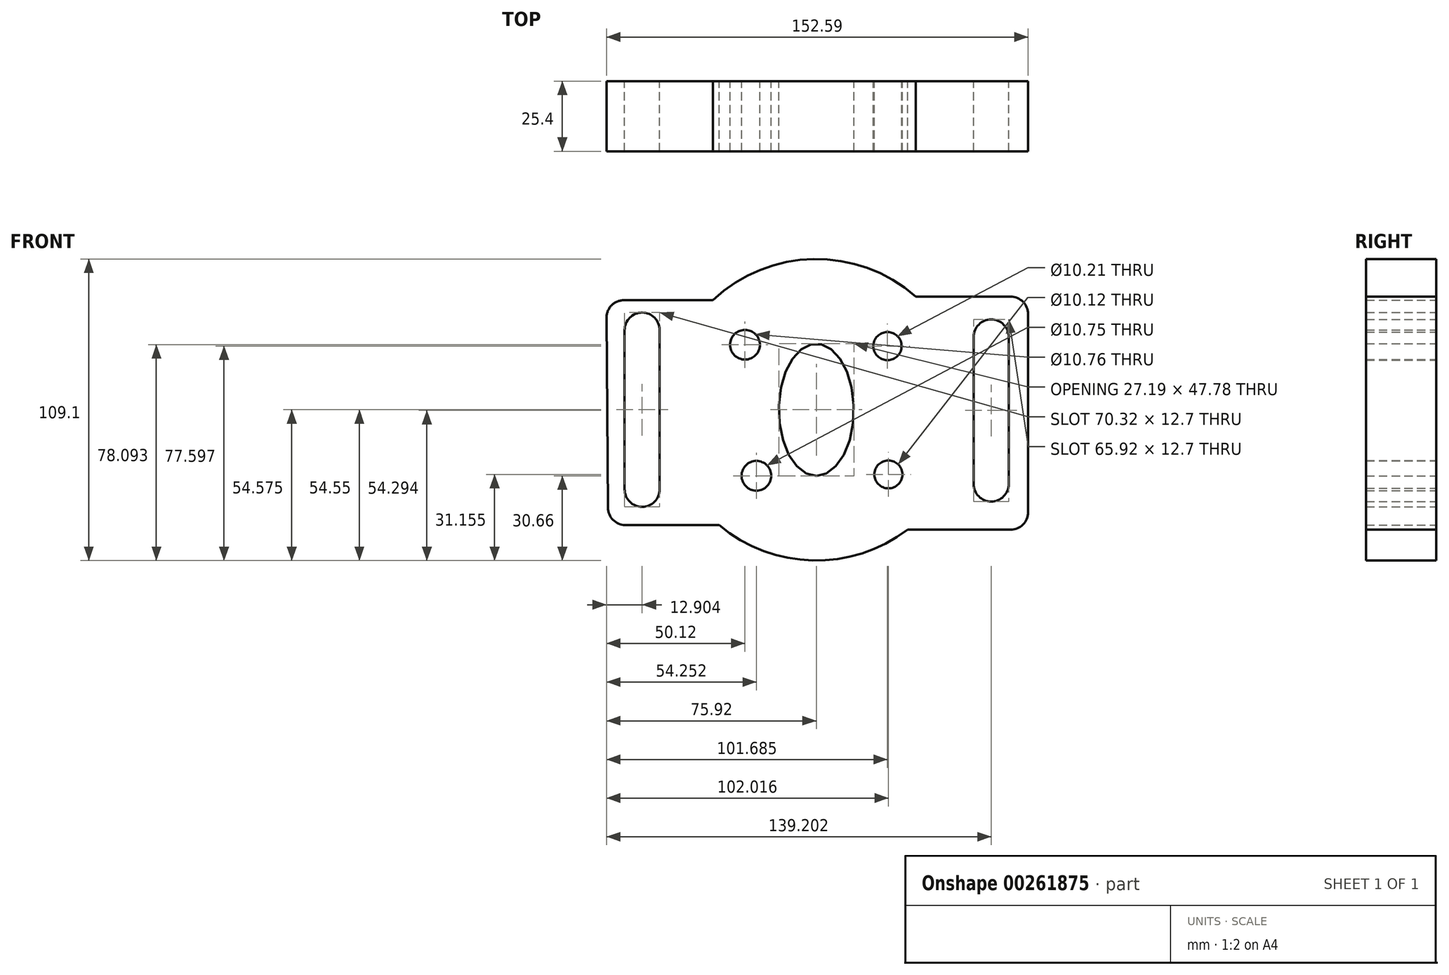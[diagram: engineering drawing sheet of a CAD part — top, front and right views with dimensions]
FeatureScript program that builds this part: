
annotation { "Feature Type Name" : "Feature", "Feature Type Description" : "" }
export const myFeature = defineFeature(function(context is Context, id is Id, definition is map)
    precondition{}
    {
        {
            var Q0;
            Q0=qCreatedBy(makeId("Front.planeOp"),FACE);
            var sketch = newSketch(context, id + "F0", { "sketchPlane" : qUnion([Q0])});
            skEllipse(sketch, "E0", {"center": v(0, 0) * mm, "majorRadius": 23.9 * mm, "minorRadius": 13.6 * mm, "majorAxis": v(0, -1)});
            skCircle(sketch, "E1", {"center": v(25.77, 23.05) * mm, "radius": 5.1 * mm});
            skCircle(sketch, "E2", {"center": v(26.1, -23.4) * mm, "radius": 5.06 * mm});
            skCircle(sketch, "E3", {"center": v(-21.67, -23.9) * mm, "radius": 5.38 * mm});
            skCircle(sketch, "E4", {"center": v(-25.8, 23.54) * mm, "radius": 5.38 * mm});
            skArc(sketch, "E5", {"start": v(36.05, 40.94) * mm, "mid": v(-0.94, 54.54) * mm, "end": v(-37.43, 39.68) * mm});
            skLineSegment(sketch, "E6", {"start": v(36.05, 40.94) * mm, "end": v(70.32, 40.94) * mm});
            skLineSegment(sketch, "E7", {"start": v(76.67, 34.59) * mm, "end": v(76.67, -37.04) * mm});
            skLineSegment(sketch, "E8", {"start": v(70.32, -43.4) * mm, "end": v(33.06, -43.4) * mm});
            skLineSegment(sketch, "E9", {"start": v(63.28, 26.35) * mm, "end": v(63.28, -26.87) * mm});
            skArc(sketch, "E10.0.startCap", {"start": v(56.93, 26.35) * mm, "mid": v(63.28, 32.7) * mm, "end": v(69.63, 26.35) * mm});
            skArc(sketch, "E10.0.endCap", {"start": v(69.63, -26.87) * mm, "mid": v(63.28, -33.22) * mm, "end": v(56.93, -26.87) * mm});
            skLineSegment(sketch, "E10.0.left", {"start": v(69.63, 26.35) * mm, "end": v(69.63, -26.87) * mm});
            skLineSegment(sketch, "E10.0.right", {"start": v(56.93, 26.35) * mm, "end": v(56.93, -26.87) * mm});
            skPoint(sketch, "E11.visualSharp", {"position": v(76.67, 40.94) * mm});
            skArc(sketch, "E11.filletArc", {"start": v(76.67, 34.59) * mm, "mid": v(74.8, 39.08) * mm, "end": v(70.32, 40.94) * mm});
            skPoint(sketch, "E12.visualSharp", {"position": v(76.67, -43.4) * mm});
            skArc(sketch, "E12.filletArc", {"start": v(70.32, -43.4) * mm, "mid": v(74.8, -41.53) * mm, "end": v(76.67, -37.04) * mm});
            skLineSegment(sketch, "E13", {"start": v(-35.16, -41.7) * mm, "end": v(-69.1, -41.7) * mm});
            skLineSegment(sketch, "E14", {"start": v(-37.43, 39.68) * mm, "end": v(-69.57, 39.68) * mm});
            skLineSegment(sketch, "E15", {"start": v(-75.92, 33.28) * mm, "end": v(-75.45, -35.4) * mm});
            skLineSegment(sketch, "E16", {"start": v(-63.02, 28.83) * mm, "end": v(-63.02, -28.78) * mm});
            skArc(sketch, "E17.0.startCap", {"start": v(-69.37, 28.83) * mm, "mid": v(-63.02, 35.18) * mm, "end": v(-56.67, 28.83) * mm});
            skArc(sketch, "E17.0.endCap", {"start": v(-56.67, -28.78) * mm, "mid": v(-63.02, -35.13) * mm, "end": v(-69.37, -28.78) * mm});
            skLineSegment(sketch, "E17.0.left", {"start": v(-56.67, 28.83) * mm, "end": v(-56.67, -28.78) * mm});
            skLineSegment(sketch, "E17.0.right", {"start": v(-69.37, 28.83) * mm, "end": v(-69.37, -28.78) * mm});
            skPoint(sketch, "E18.visualSharp", {"position": v(-75.4, -41.7) * mm});
            skArc(sketch, "E18.filletArc", {"start": v(-75.45, -35.4) * mm, "mid": v(-73.57, -39.86) * mm, "end": v(-69.1, -41.7) * mm});
            skPoint(sketch, "E19.visualSharp", {"position": v(-75.97, 39.68) * mm});
            skArc(sketch, "E19.filletArc", {"start": v(-69.57, 39.68) * mm, "mid": v(-74.08, 37.8) * mm, "end": v(-75.92, 33.28) * mm});
            skArc(sketch, "E20.trimOffspring", {"start": v(-35.16, -41.7) * mm, "mid": v(-1.35, -54.53) * mm, "end": v(33.06, -43.4) * mm});
            skSolve(sketch);
        }
        {
            var Q0;
            Q0=makeQuery(id+"F0.imprint","IMPRINT",FACE,{"disambiguationData":[TD([[makeQuery(id+"F0.imprint","IMPRINT",EDGE,{"derivedFrom":sQuery(id+"F0.wireOp",EDGE,"E0")}),-1.0]])]});
            extrude(context, id + "F1", {"entities" : qUnion([Q0]), "depth" : 25.4 * mm});
        }
    });
